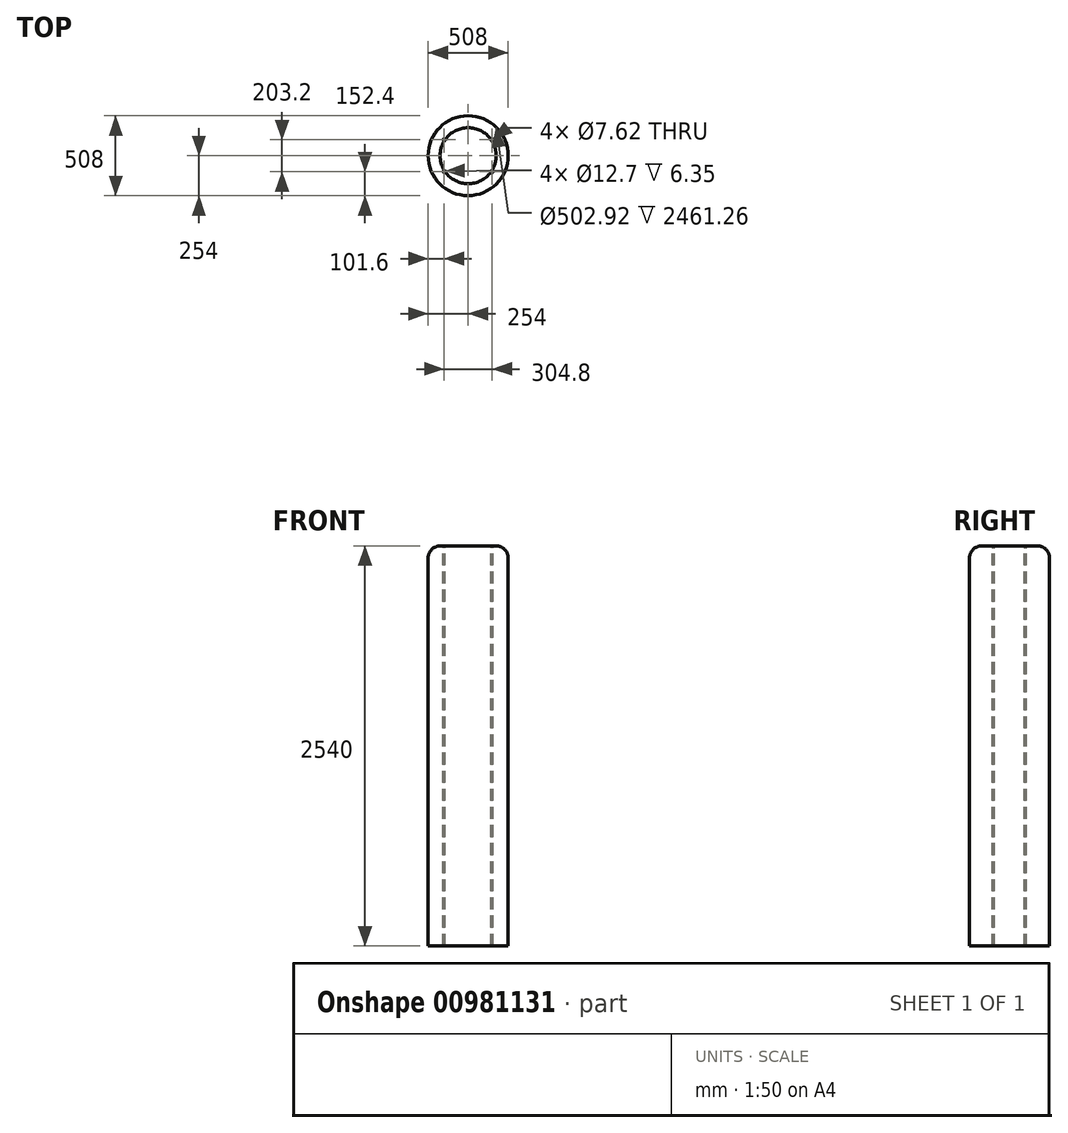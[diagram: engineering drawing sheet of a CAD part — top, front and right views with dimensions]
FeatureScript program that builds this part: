
annotation { "Feature Type Name" : "Feature", "Feature Type Description" : "" }
export const myFeature = defineFeature(function(context is Context, id is Id, definition is map)
    precondition{}
    {
        {
            var Q0;
            Q0=qCreatedBy(makeId("Top.planeOp"),FACE);
            var sketch = newSketch(context, id + "F0", { "sketchPlane" : qUnion([Q0])});
            skCircle(sketch, "E0", {"center": v(0, 0) * mm, "radius": 254 * mm});
            skSolve(sketch);
        }
        {
            var Q0;
            Q0=makeQuery(id+"F0.imprint","IMPRINT",FACE,{"disambiguationData":[TD([[makeQuery(id+"F0.imprint","IMPRINT",EDGE,{"derivedFrom":sQuery(id+"F0.wireOp",EDGE,"E0")}),1.0]])]});
            extrude(context, id + "F1", {"entities" : qUnion([Q0]), "depth" : 2540 * mm, "offsetDistance" : 25.4 * mm});
        }
        {
            var Q0;
            Q0=makeQuery(id+"F1.opExtrude","CAP_FACE",FACE,{"disambiguationData":[OSD([sQuery(id+"F0.wireOp",EDGE,"E0")])],"isStart":false});
            var sketch = newSketch(context, id + "F2", { "sketchPlane" : qUnion([Q0])});
            skLineSegment(sketch, "E1.bottom", {"start": v(152.4, -101.6) * mm, "end": v(-152.4, -101.6) * mm});
            skLineSegment(sketch, "E1.top", {"start": v(152.4, 101.6) * mm, "end": v(-152.4, 101.6) * mm});
            skLineSegment(sketch, "E1.left", {"start": v(152.4, -101.6) * mm, "end": v(152.4, 101.6) * mm});
            skLineSegment(sketch, "E1.right", {"start": v(-152.4, -101.6) * mm, "end": v(-152.4, 101.6) * mm});
            skPoint(sketch, "E1.middle", {"position": v(0, 0) * mm});
            skSolve(sketch);
        }
        {
            var Q0;
            Q0=makeQuery(id+"F1.opExtrude","CAP_EDGE",EDGE,{"disambiguationData":[OSD([sQuery(id+"F0.wireOp",EDGE,"E0")])],"isStart":false});
            fillet(context, id + "F3", {"entities" : qUnion([Q0]), "radius" : 76.2 * mm, "tangentPropagation" : true, "allowEdgeOverflow" : false});
        }
        {
            var Q0;
            Q0=sQuery(id+"F2.wireOp",VERTEX,"E1.right.end");
            var Q1;
            Q1=sQuery(id+"F2.wireOp",VERTEX,"E1.bottom.start");
            var Q2;
            Q2=sQuery(id+"F2.wireOp",VERTEX,"E1.left.end");
            var Q3;
            Q3=sQuery(id+"F2.wireOp",VERTEX,"E1.bottom.end");
            var Q4;
            Q4=makeQuery(id+"F1.opExtrude","SWEPT_BODY",BODY,{"disambiguationData":[OSD([sQuery(id+"F0.wireOp",EDGE,"E0")])]});
            hole(context, id + "F4", {"style" : HoleStyle.C_BORE, "endStyle" : HoleEndStyle.THROUGH, "holeDiameter" : 7.62 * mm, "cBoreDiameter" : 12.7 * mm, "cBoreDepth" : 6.35 * mm, "majorDiameter" : 6.35 * mm, "isTappedThrough" : true, "tappedDepth" : 12.7 * mm, "tapClearance" : 3, "startFromSketch" : true, "locations" : qUnion([Q0, Q1, Q2, Q3]), "scope" : qUnion([Q4])});
        }
        {
            var Q0;
            Q0=makeQuery(id+"F1.opExtrude","CAP_FACE",FACE,{"disambiguationData":[OSD([sQuery(id+"F0.wireOp",EDGE,"E0")])],"isStart":false});
            shell(context, id + "F5", {"entities" : qUnion([Q0]), "thickness" : 2.54 * mm});
        }
    });
